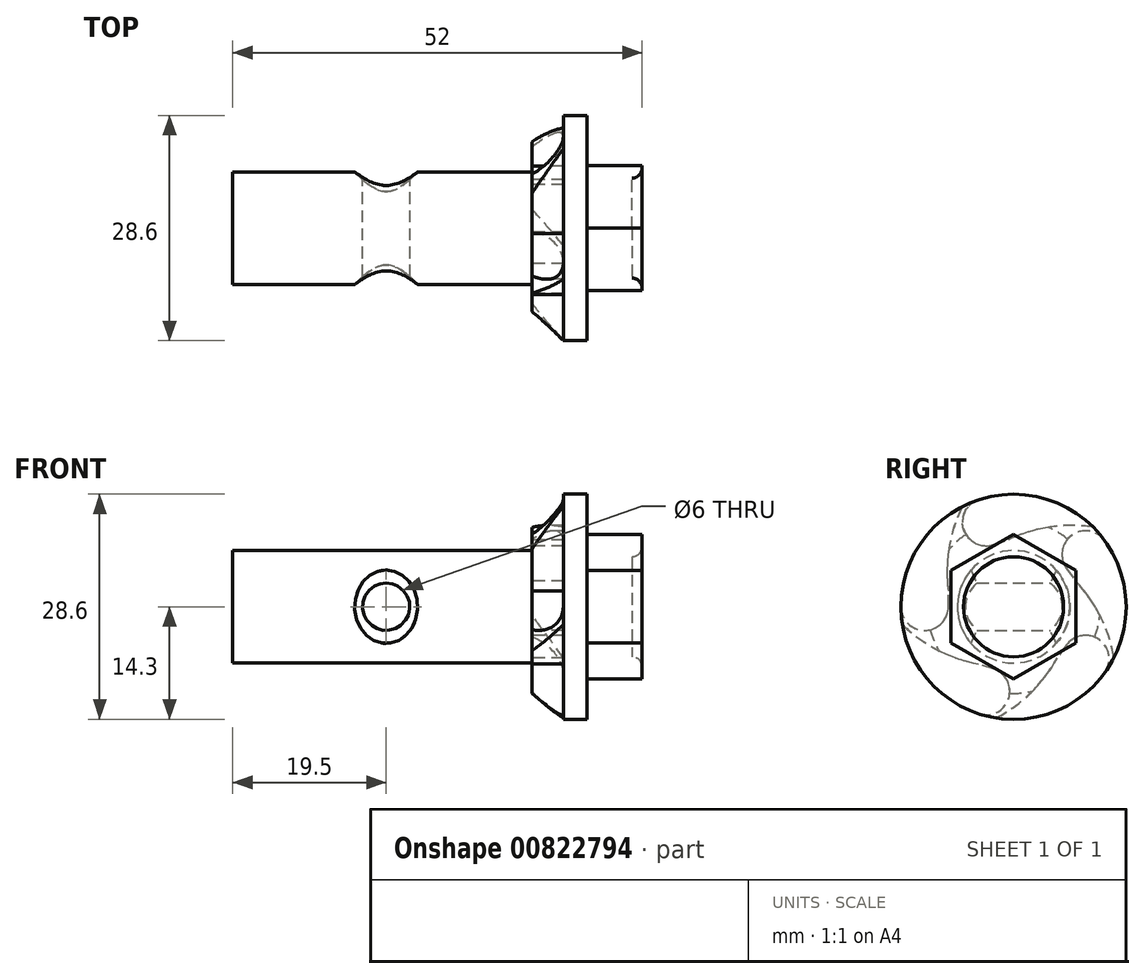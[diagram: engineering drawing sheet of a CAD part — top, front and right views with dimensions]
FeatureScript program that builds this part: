
annotation { "Feature Type Name" : "Feature", "Feature Type Description" : "" }
export const myFeature = defineFeature(function(context is Context, id is Id, definition is map)
    precondition{}
    {
        {
            var Q0;
            Q0=qCreatedBy(makeId("Front.planeOp"),FACE);
            var sketch = newSketch(context, id + "F0", { "sketchPlane" : qUnion([Q0])});
            skLineSegment(sketch, "E0", {"start": v(0, 0) * mm, "end": v(0, 7.14) * mm, "construction": true});
            skLineSegment(sketch, "E1", {"start": v(0, 7.14) * mm, "end": v(-38, 7.14) * mm});
            skLineSegment(sketch, "E2", {"start": v(-38, 7.14) * mm, "end": v(-38, 0) * mm});
            skLineSegment(sketch, "E3", {"start": v(-38, 0) * mm, "end": v(0, 0) * mm});
            skLineSegment(sketch, "E4", {"start": v(0, 7.14) * mm, "end": v(0, 11) * mm});
            skLineSegment(sketch, "E5", {"start": v(4, 14.3) * mm, "end": v(7, 14.3) * mm});
            skLineSegment(sketch, "E6", {"start": v(7, 14.3) * mm, "end": v(7, 10) * mm});
            skLineSegment(sketch, "E7", {"start": v(7, 10) * mm, "end": v(14, 10) * mm});
            skLineSegment(sketch, "E8", {"start": v(14, 10) * mm, "end": v(14, 6.35) * mm});
            skLineSegment(sketch, "E9", {"start": v(12.7, 0) * mm, "end": v(0, 0) * mm});
            skLineSegment(sketch, "E10", {"start": v(12.7, 0) * mm, "end": v(12.7, 6.35) * mm});
            skLineSegment(sketch, "E11", {"start": v(12.7, 6.35) * mm, "end": v(14, 6.35) * mm});
            skPoint(sketch, "E12.orphan", {"position": v(14, 0) * mm});
            skLineSegment(sketch, "E13", {"start": v(4, 14.3) * mm, "end": v(0, 11) * mm});
            skSolve(sketch);
        }
        {
            var Q0;
            Q0 = qSketchRegion(id + "F0", true);
            var Q1;
            Q1=sQuery(id+"F0.wireOp",EDGE,"E3");
            revolve(context, id + "F1", {"surfaceOperationType" : NewSurfaceOperationType.NEW, "entities" : qUnion([Q0]), "axis" : qUnion([Q1]), "revolveType" : RevolveType.FULL});
        }
        {
            var Q0;
            Q0=makeQuery(id+"F1.opRevolve","SWEPT_FACE",FACE,{"disambiguationData":[OSD([sQuery(id+"F0.wireOp",EDGE,"E8")])]});
            var sketch = newSketch(context, id + "F2", { "sketchPlane" : qUnion([Q0])});
            skCircle(sketch, "E14.cCircle", {"center": v(0, 0) * mm, "radius": 7.94 * mm, "construction": true});
            skLineSegment(sketch, "E14.0", {"start": v(-7.94, -4.58) * mm, "end": v(-7.94, 4.58) * mm});
            skLineSegment(sketch, "E14.1", {"start": v(-7.94, 4.58) * mm, "end": v(0, 9.17) * mm});
            skLineSegment(sketch, "E14.2", {"start": v(0, 9.17) * mm, "end": v(7.94, 4.58) * mm});
            skLineSegment(sketch, "E14.3", {"start": v(7.94, 4.58) * mm, "end": v(7.94, -4.58) * mm});
            skLineSegment(sketch, "E14.4", {"start": v(7.94, -4.58) * mm, "end": v(0, -9.17) * mm});
            skLineSegment(sketch, "E14.5", {"start": v(0, -9.17) * mm, "end": v(-7.94, -4.58) * mm});
            skPoint(sketch, "E14.0.midPoint", {"position": v(-7.94, 0) * mm});
            skCircle(sketch, "E15", {"center": v(0, 0) * mm, "radius": 11.06 * mm});
            skSolve(sketch);
        }
        {
            var Q0;
            Q0 = qSketchRegion(id + "F2", true);
            var Q1;
            Q1=makeQuery(id+"F1.opRevolve","SWEPT_FACE",FACE,{"disambiguationData":[OSD([sQuery(id+"F0.wireOp",EDGE,"E6")])]});
            extrude(context, id + "F3", {"entities" : qUnion([Q0]), "operationType" : NewBodyOperationType.REMOVE, "endBound" : BoundingType.UP_TO_SURFACE, "oppositeDirection" : true, "depth" : 25 * mm, "endBoundEntityFace" : qUnion([Q1]), "offsetDistance" : 25 * mm});
        }
        {
            var Q0;
            Q0=makeQuery(id+"F1.opRevolve","SWEPT_EDGE",EDGE,{"disambiguationData":[OSD([sQuery(id+"F0.wireOp",EDGE,"E8"),sQuery(id+"F0.wireOp",EDGE,"E11")])]});
            fillet(context, id + "F4", {"entities" : qUnion([Q0]), "radius" : 1.3 * mm, "tangentPropagation" : true, "allowEdgeOverflow" : false});
        }
        {
            var Q0;
            Q0=makeQuery(id+"F1.opRevolve","SWEPT_FACE",FACE,{"disambiguationData":[OSD([sQuery(id+"F0.wireOp",EDGE,"E4")])]});
            var sketch = newSketch(context, id + "F5", { "sketchPlane" : qUnion([Q0])});
            skLineSegment(sketch, "E16", {"start": v(0, 0) * mm, "end": v(6.51, 12.73) * mm, "construction": true});
            skCircle(sketch, "E17.0", {"center": v(0, 0) * mm, "radius": 14.3 * mm, "construction": true});
            skLineSegment(sketch, "E18", {"start": v(0, 0) * mm, "end": v(14.3, 0) * mm, "construction": true});
            skLineSegment(sketch, "E19", {"start": v(14.3, 0) * mm, "end": v(8.3, 0) * mm, "construction": true});
            skArc(sketch, "E20", {"start": v(8.3, 0) * mm, "mid": v(11.3, -3) * mm, "end": v(14.3, 0) * mm});
            skLineSegment(sketch, "E21", {"start": v(8.3, 0) * mm, "end": v(8.3, 2) * mm});
            skArc(sketch, "E22", {"start": v(8.3, 2) * mm, "mid": v(8.2, 7.5) * mm, "end": v(6.51, 12.73) * mm});
            skLineSegment(sketch, "E23", {"start": v(14.3, 0) * mm, "end": v(16.26, 0) * mm});
            skLineSegment(sketch, "E24", {"start": v(16.26, 0) * mm, "end": v(16.26, 14.17) * mm});
            skLineSegment(sketch, "E25", {"start": v(16.26, 14.17) * mm, "end": v(6.51, 14.25) * mm});
            skLineSegment(sketch, "E26", {"start": v(6.51, 14.25) * mm, "end": v(6.51, 12.73) * mm});
            skLineSegment(sketch, "E27.1.0", {"start": v(-11.54, 10.6) * mm, "end": v(-10.1, 10.13) * mm});
            skLineSegment(sketch, "E27.1.1", {"start": v(-8.45, 19.84) * mm, "end": v(-11.54, 10.6) * mm});
            skArc(sketch, "E27.1.2", {"start": v(2.56, 7.9) * mm, "mid": v(6.35, 9.82) * mm, "end": v(4.42, 13.6) * mm});
            skLineSegment(sketch, "E27.1.3", {"start": v(2.56, 7.9) * mm, "end": v(0.66, 8.51) * mm});
            skLineSegment(sketch, "E27.1.4", {"start": v(5.03, 15.47) * mm, "end": v(-8.45, 19.84) * mm});
            skLineSegment(sketch, "E27.1.5", {"start": v(4.42, 13.6) * mm, "end": v(5.03, 15.47) * mm});
            skArc(sketch, "E27.1.6", {"start": v(0.66, 8.51) * mm, "mid": v(-4.6, 10.12) * mm, "end": v(-10.1, 10.13) * mm});
            skLineSegment(sketch, "E27.2.0", {"start": v(-13.64, -7.7) * mm, "end": v(-12.75, -6.47) * mm});
            skLineSegment(sketch, "E27.2.1", {"start": v(-21.48, -1.9) * mm, "end": v(-13.64, -7.7) * mm});
            skArc(sketch, "E27.2.2", {"start": v(-6.71, 4.88) * mm, "mid": v(-7.38, 9.07) * mm, "end": v(-11.57, 8.4) * mm});
            skLineSegment(sketch, "E27.2.3", {"start": v(-6.71, 4.88) * mm, "end": v(-7.9, 3.26) * mm});
            skLineSegment(sketch, "E27.2.4", {"start": v(-13.16, 9.56) * mm, "end": v(-21.48, -1.9) * mm});
            skLineSegment(sketch, "E27.2.5", {"start": v(-11.57, 8.4) * mm, "end": v(-13.16, 9.56) * mm});
            skArc(sketch, "E27.2.6", {"start": v(-7.9, 3.26) * mm, "mid": v(-11.05, -1.24) * mm, "end": v(-12.75, -6.47) * mm});
            skLineSegment(sketch, "E27.3.0", {"start": v(3.1, -15.35) * mm, "end": v(2.22, -14.13) * mm});
            skLineSegment(sketch, "E27.3.1", {"start": v(-4.83, -21.02) * mm, "end": v(3.1, -15.35) * mm});
            skArc(sketch, "E27.3.2", {"start": v(-6.71, -4.88) * mm, "mid": v(-10.9, -4.21) * mm, "end": v(-11.57, -8.4) * mm});
            skLineSegment(sketch, "E27.3.3", {"start": v(-6.71, -4.88) * mm, "end": v(-5.54, -6.5) * mm});
            skLineSegment(sketch, "E27.3.4", {"start": v(-13.16, -9.56) * mm, "end": v(-4.83, -21.02) * mm});
            skLineSegment(sketch, "E27.3.5", {"start": v(-11.57, -8.4) * mm, "end": v(-13.16, -9.56) * mm});
            skArc(sketch, "E27.3.6", {"start": v(-5.54, -6.5) * mm, "mid": v(-2.23, -10.89) * mm, "end": v(2.22, -14.13) * mm});
            skLineSegment(sketch, "E27.4.0", {"start": v(15.56, -1.79) * mm, "end": v(14.12, -2.26) * mm});
            skLineSegment(sketch, "E27.4.1", {"start": v(18.5, -11.09) * mm, "end": v(15.56, -1.79) * mm});
            skArc(sketch, "E27.4.2", {"start": v(2.56, -7.9) * mm, "mid": v(0.64, -11.67) * mm, "end": v(4.42, -13.6) * mm});
            skLineSegment(sketch, "E27.4.3", {"start": v(2.56, -7.9) * mm, "end": v(4.47, -7.28) * mm});
            skLineSegment(sketch, "E27.4.4", {"start": v(5.03, -15.47) * mm, "end": v(18.5, -11.09) * mm});
            skLineSegment(sketch, "E27.4.5", {"start": v(4.42, -13.6) * mm, "end": v(5.03, -15.47) * mm});
            skArc(sketch, "E27.4.6", {"start": v(4.47, -7.28) * mm, "mid": v(9.67, -5.49) * mm, "end": v(14.12, -2.26) * mm});
            skSolve(sketch);
        }
        {
            var Q0;
            Q0 = qSketchRegion(id + "F5", true);
            extrude(context, id + "F6", {"entities" : qUnion([Q0]), "operationType" : NewBodyOperationType.REMOVE, "oppositeDirection" : true, "depth" : 4 * mm, "offsetDistance" : 25 * mm});
        }
        {
            var Q0;
            Q0=qCreatedBy(makeId("Front.planeOp"),FACE);
            var sketch = newSketch(context, id + "F7", { "sketchPlane" : qUnion([Q0])});
            skLineSegment(sketch, "E28", {"start": v(0, 0) * mm, "end": v(-18.5, 0) * mm, "construction": true});
            skCircle(sketch, "E29", {"center": v(-18.5, 0) * mm, "radius": 3 * mm});
            skSolve(sketch);
        }
        {
            var Q0;
            Q0 = qSketchRegion(id + "F7", true);
            extrude(context, id + "F8", {"entities" : qUnion([Q0]), "operationType" : NewBodyOperationType.REMOVE, "endBound" : BoundingType.SYMMETRIC, "depth" : 25 * mm, "offsetDistance" : 25 * mm});
        }
        {
            var Q0;
            Q0=makeQuery(id+"F8.boolean.opBoolean","COPY",FACE,{"derivedFrom":makeQuery(id+"F8.opExtrude","SWEPT_FACE",FACE,{"disambiguationData":[OSD([sQuery(id+"F7.wireOp",EDGE,"E29")])]})});
            chamfer(context, id + "F9", {"entities" : qUnion([Q0]), "width" : 1 * mm, "tangentPropagation" : true});
        }
    });
